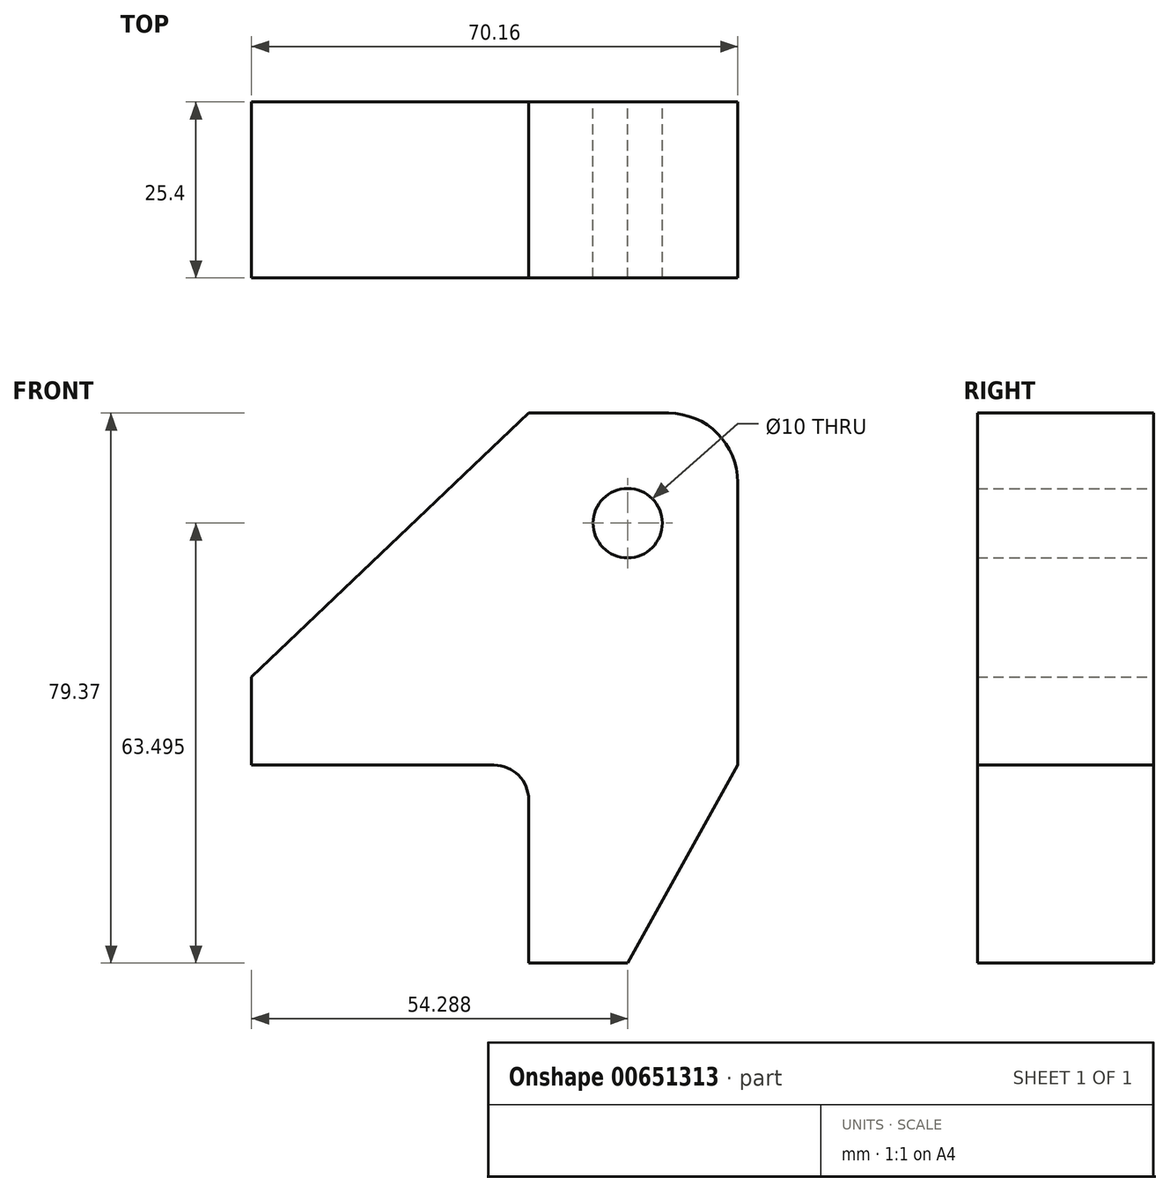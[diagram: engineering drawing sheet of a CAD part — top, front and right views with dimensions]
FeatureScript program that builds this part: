
annotation { "Feature Type Name" : "Feature", "Feature Type Description" : "" }
export const myFeature = defineFeature(function(context is Context, id is Id, definition is map)
    precondition{}
    {
        {
            var Q0;
            Q0=qCreatedBy(makeId("Front.planeOp"),FACE);
            var sketch = newSketch(context, id + "F0", { "sketchPlane" : qUnion([Q0])});
            skLineSegment(sketch, "E0.bottom", {"start": v(0, 0) * mm, "end": v(14.29, 0) * mm});
            skLineSegment(sketch, "E0.top", {"start": v(0, -28.57) * mm, "end": v(14.29, -28.57) * mm});
            skLineSegment(sketch, "E0.left", {"start": v(0, 0) * mm, "end": v(0, -28.57) * mm});
            skLineSegment(sketch, "E0.right", {"start": v(14.29, 0) * mm, "end": v(14.29, -28.58) * mm});
            skLineSegment(sketch, "E1.bottom", {"start": v(0, 0) * mm, "end": v(-40, 0) * mm});
            skLineSegment(sketch, "E1.top", {"start": v(0, 12.7) * mm, "end": v(-40, 12.7) * mm});
            skLineSegment(sketch, "E1.left", {"start": v(0, 0) * mm, "end": v(0, 12.7) * mm});
            skLineSegment(sketch, "E1.right", {"start": v(-40, 0) * mm, "end": v(-40, 12.7) * mm});
            skLineSegment(sketch, "E2.top", {"start": v(0, 50.8) * mm, "end": v(14.29, 50.8) * mm});
            skLineSegment(sketch, "E2.left", {"start": v(0, 0) * mm, "end": v(0, 50.8) * mm});
            skLineSegment(sketch, "E2.right", {"start": v(14.29, 0) * mm, "end": v(14.29, 50.8) * mm});
            skCircle(sketch, "E3", {"center": v(14.29, 34.93) * mm, "radius": 5 * mm});
            skLineSegment(sketch, "E4.bottom", {"start": v(14.29, 50.8) * mm, "end": v(14.29, 50.8) * mm});
            skLineSegment(sketch, "E4.top", {"start": v(14.29, 0) * mm, "end": v(14.29, 0) * mm});
            skLineSegment(sketch, "E4.left", {"start": v(14.29, 50.8) * mm, "end": v(14.29, 0) * mm});
            skLineSegment(sketch, "E4.right", {"start": v(14.29, 50.8) * mm, "end": v(14.29, 0) * mm});
            skLineSegment(sketch, "E5.bottom", {"start": v(14.29, 0) * mm, "end": v(30.16, 0) * mm});
            skLineSegment(sketch, "E5.top", {"start": v(14.29, 50.8) * mm, "end": v(30.16, 50.8) * mm});
            skLineSegment(sketch, "E5.right", {"start": v(30.16, 0) * mm, "end": v(30.16, 50.8) * mm});
            skLineSegment(sketch, "E6", {"start": v(30.16, 0) * mm, "end": v(14.29, -28.57) * mm});
            skLineSegment(sketch, "E7", {"start": v(0, 50.8) * mm, "end": v(-40, 12.7) * mm});
            skSolve(sketch);
        }
        {
            var Q0;
            {var subQ1=sQuery(id+"F0.wireOp",EDGE,"E5.bottom");Q0=makeQuery(id+"F0.imprint","IMPRINT",FACE,{"disambiguationData":[TD([[makeQuery(id+"F0.imprint","IMPRINT",EDGE,{"derivedFrom":subQ1}),1.0]])]});}
            var Q1;
            {var subQ3=sQuery(id+"F0.wireOp",EDGE,"E0.bottom");Q1=makeQuery(id+"F0.imprint","IMPRINT",FACE,{"disambiguationData":[TD([[makeQuery(id+"F0.imprint","IMPRINT",EDGE,{"derivedFrom":subQ3}),1.0]])]});}
            var Q2;
            {var subQ0=sQuery(id+"F0.wireOp",EDGE,"E1.top");Q2=makeQuery(id+"F0.imprint","IMPRINT",FACE,{"disambiguationData":[TD([[makeQuery(id+"F0.imprint","IMPRINT",EDGE,{"derivedFrom":subQ0}),-1.0]])]});}
            var Q3;
            {var subQ0=sQuery(id+"F0.wireOp",EDGE,"E1.bottom");Q3=makeQuery(id+"F0.imprint","IMPRINT",FACE,{"disambiguationData":[TD([[makeQuery(id+"F0.imprint","IMPRINT",EDGE,{"derivedFrom":subQ0}),-1.0]])]});}
            var Q4;
            Q4=makeQuery(id+"F0.imprint","IMPRINT",FACE,{"disambiguationData":[TD([[makeQuery(id+"F0.imprint","IMPRINT",EDGE,{"derivedFrom":sQuery(id+"F0.wireOp",EDGE,"E0.top")}),1.0]])]});
            var Q5;
            Q5=makeQuery(id+"F0.imprint","IMPRINT",FACE,{"disambiguationData":[TD([[makeQuery(id+"F0.imprint","IMPRINT",EDGE,{"derivedFrom":sQuery(id+"F0.wireOp",EDGE,"E0.right")}),1.0]])]});
            extrude(context, id + "F1", {"entities" : qUnion([Q0, Q1, Q2, Q3, Q4, Q5]), "depth" : 25.4 * mm, "offsetDistance" : 25 * mm});
        }
        {
            var Q0;
            Q0=makeQuery(id+"F1.opExtrude","SWEPT_EDGE",EDGE,{"disambiguationData":[OSD([sQuery(id+"F0.wireOp",EDGE,"E5.top"),sQuery(id+"F0.wireOp",EDGE,"E5.right")])]});
            fillet(context, id + "F2", {"entities" : qUnion([Q0]), "radius" : 10 * mm, "tangentPropagation" : true, "allowEdgeOverflow" : false});
        }
        {
            var Q0;
            Q0=makeQuery(id+"F1.opExtrude","SWEPT_EDGE",EDGE,{"disambiguationData":[OSD([sQuery(id+"F0.wireOp",EDGE,"E0.left"),sQuery(id+"F0.wireOp",EDGE,"E1.bottom"),sQuery(id+"F0.wireOp",EDGE,"E0.bottom"),sQuery(id+"F0.wireOp",EDGE,"E2.left")])]});
            fillet(context, id + "F3", {"entities" : qUnion([Q0]), "radius" : 5 * mm, "tangentPropagation" : true, "allowEdgeOverflow" : false});
        }
    });
